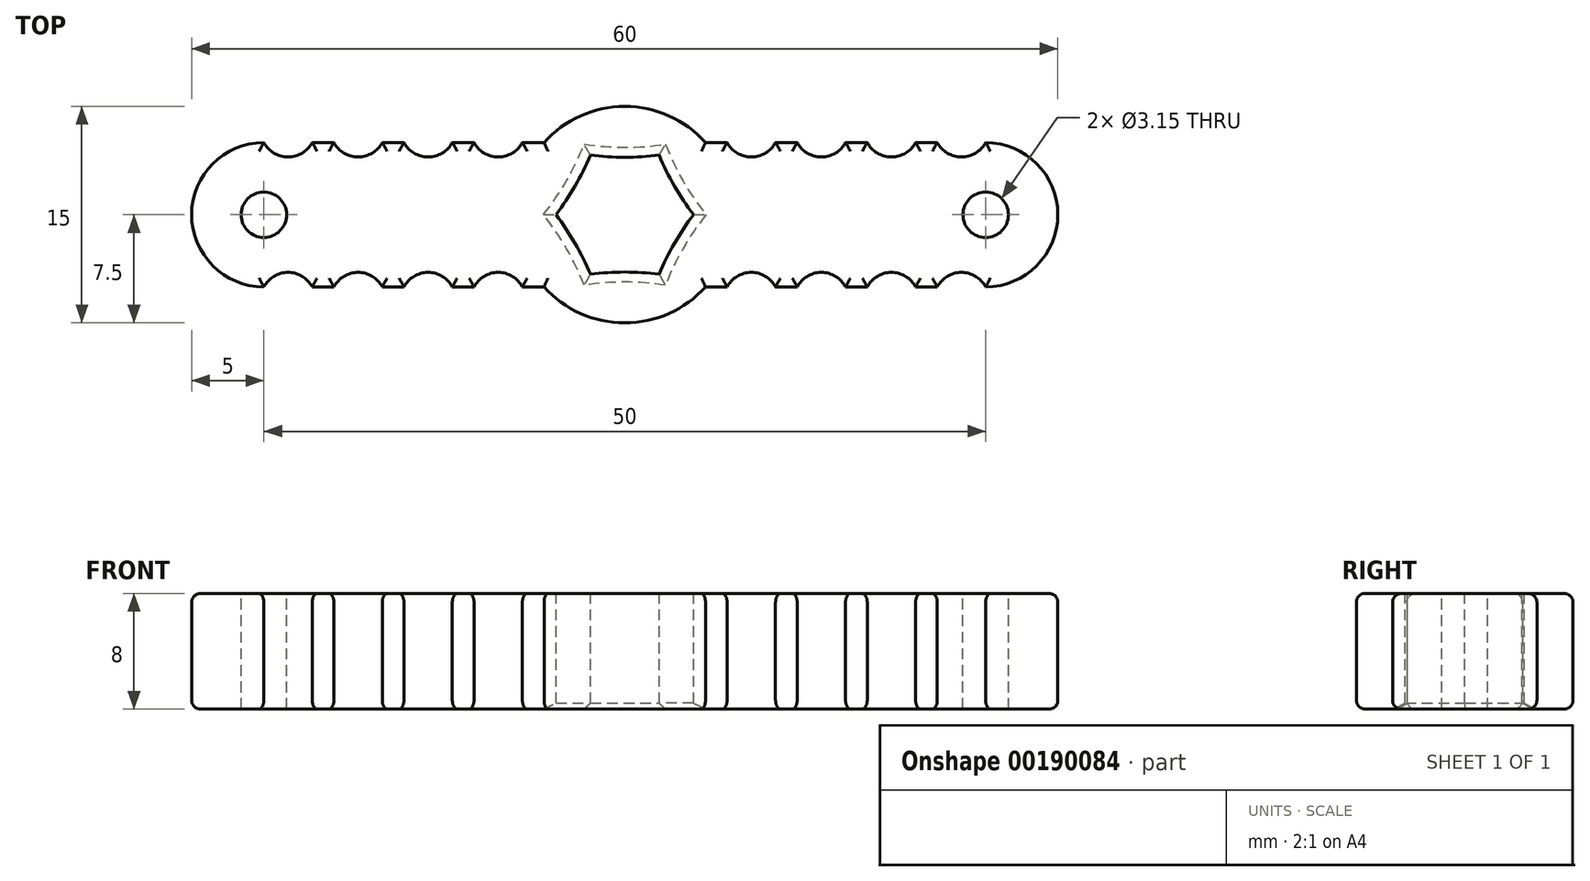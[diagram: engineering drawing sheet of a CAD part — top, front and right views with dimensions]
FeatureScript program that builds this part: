
annotation { "Feature Type Name" : "Feature", "Feature Type Description" : "" }
export const myFeature = defineFeature(function(context is Context, id is Id, definition is map)
    precondition{}
    {
        {
            var Q0;
            Q0=qCreatedBy(makeId("Top.planeOp"),FACE);
            var sketch = newSketch(context, id + "F0", { "sketchPlane" : qUnion([Q0])});
            skLineSegment(sketch, "E0", {"start": v(0, 7.5) * mm, "end": v(0, 0) * mm, "construction": true});
            skLineSegment(sketch, "E1", {"start": v(0, 0) * mm, "end": v(30, 0) * mm, "construction": true});
            skArc(sketch, "E2", {"start": v(30, 0) * mm, "mid": v(28.54, 3.54) * mm, "end": v(25, 5) * mm});
            skArc(sketch, "E3", {"start": v(5.6, 5) * mm, "mid": v(3.06, 6.85) * mm, "end": v(0, 7.5) * mm});
            skLineSegment(sketch, "E4", {"start": v(5.6, 5) * mm, "end": v(7.1, 5) * mm});
            skArc(sketch, "E5", {"start": v(7.1, 5) * mm, "mid": v(8.77, 4) * mm, "end": v(10.44, 5) * mm});
            skLineSegment(sketch, "E6.1.0.0", {"start": v(10.44, 5) * mm, "end": v(11.94, 5) * mm});
            skArc(sketch, "E6.1.0.1", {"start": v(11.94, 5) * mm, "mid": v(13.62, 4) * mm, "end": v(15.3, 5) * mm});
            skLineSegment(sketch, "E6.2.0.0", {"start": v(15.3, 5) * mm, "end": v(16.8, 5) * mm});
            skArc(sketch, "E6.2.0.1", {"start": v(16.8, 5) * mm, "mid": v(18.47, 4) * mm, "end": v(20.15, 5) * mm});
            skLineSegment(sketch, "E6.direction1", {"start": v(5.6, 5) * mm, "end": v(10.44, 5) * mm, "construction": true});
            skLineSegment(sketch, "E7.0.3.0", {"start": v(20.15, 5) * mm, "end": v(21.65, 5) * mm});
            skArc(sketch, "E7.3.3.0", {"start": v(21.65, 5) * mm, "mid": v(23.32, 4) * mm, "end": v(25, 5) * mm});
            skArc(sketch, "E8.MirrorCS", {"start": v(30, 0) * mm, "mid": v(28.54, -3.54) * mm, "end": v(25, -5) * mm});
            skArc(sketch, "E9.MirrorCS", {"start": v(21.65, -5) * mm, "mid": v(23.32, -4) * mm, "end": v(25, -5) * mm});
            skLineSegment(sketch, "E10.MirrorCS", {"start": v(20.15, -5) * mm, "end": v(21.65, -5) * mm});
            skArc(sketch, "E11.MirrorCS", {"start": v(16.8, -5) * mm, "mid": v(18.47, -4) * mm, "end": v(20.15, -5) * mm});
            skLineSegment(sketch, "E12.MirrorCS", {"start": v(15.3, -5) * mm, "end": v(16.8, -5) * mm});
            skArc(sketch, "E13.MirrorCS", {"start": v(11.94, -5) * mm, "mid": v(13.62, -4) * mm, "end": v(15.3, -5) * mm});
            skLineSegment(sketch, "E14.MirrorCS", {"start": v(10.44, -5) * mm, "end": v(11.94, -5) * mm});
            skLineSegment(sketch, "E15.MirrorCS", {"start": v(5.6, -5) * mm, "end": v(7.1, -5) * mm});
            skArc(sketch, "E16.MirrorCS", {"start": v(7.1, -5) * mm, "mid": v(8.77, -4) * mm, "end": v(10.44, -5) * mm});
            skArc(sketch, "E17.MirrorCS", {"start": v(5.6, -5) * mm, "mid": v(3.06, -6.85) * mm, "end": v(0, -7.5) * mm});
            skArc(sketch, "E18.MirrorCS", {"start": v(-5.6, 5) * mm, "mid": v(-3.06, 6.85) * mm, "end": v(0, 7.5) * mm});
            skLineSegment(sketch, "E19.MirrorCS", {"start": v(-5.6, 5) * mm, "end": v(-7.1, 5) * mm});
            skArc(sketch, "E20.MirrorCS", {"start": v(-7.1, 5) * mm, "mid": v(-8.77, 4) * mm, "end": v(-10.44, 5) * mm});
            skLineSegment(sketch, "E21.MirrorCS", {"start": v(-10.44, 5) * mm, "end": v(-11.94, 5) * mm});
            skArc(sketch, "E22.MirrorCS", {"start": v(-11.94, 5) * mm, "mid": v(-13.62, 4) * mm, "end": v(-15.3, 5) * mm});
            skLineSegment(sketch, "E23.MirrorCS", {"start": v(-15.3, 5) * mm, "end": v(-16.8, 5) * mm});
            skArc(sketch, "E24.MirrorCS", {"start": v(-16.8, 5) * mm, "mid": v(-18.47, 4) * mm, "end": v(-20.15, 5) * mm});
            skLineSegment(sketch, "E25.MirrorCS", {"start": v(-20.15, 5) * mm, "end": v(-21.65, 5) * mm});
            skArc(sketch, "E26.MirrorCS", {"start": v(-21.65, 5) * mm, "mid": v(-23.32, 4) * mm, "end": v(-25, 5) * mm});
            skArc(sketch, "E27.MirrorCS", {"start": v(-30, 0) * mm, "mid": v(-28.54, 3.54) * mm, "end": v(-25, 5) * mm});
            skArc(sketch, "E28.MirrorCS", {"start": v(-30, 0) * mm, "mid": v(-28.54, -3.54) * mm, "end": v(-25, -5) * mm});
            skArc(sketch, "E29.MirrorCS", {"start": v(-21.65, -5) * mm, "mid": v(-23.32, -4) * mm, "end": v(-25, -5) * mm});
            skLineSegment(sketch, "E30.MirrorCS", {"start": v(-20.15, -5) * mm, "end": v(-21.65, -5) * mm});
            skArc(sketch, "E31.MirrorCS", {"start": v(-16.8, -5) * mm, "mid": v(-18.47, -4) * mm, "end": v(-20.15, -5) * mm});
            skLineSegment(sketch, "E32.MirrorCS", {"start": v(-15.3, -5) * mm, "end": v(-16.8, -5) * mm});
            skArc(sketch, "E33.MirrorCS", {"start": v(-11.94, -5) * mm, "mid": v(-13.62, -4) * mm, "end": v(-15.3, -5) * mm});
            skLineSegment(sketch, "E34.MirrorCS", {"start": v(-10.44, -5) * mm, "end": v(-11.94, -5) * mm});
            skArc(sketch, "E35.MirrorCS", {"start": v(-7.1, -5) * mm, "mid": v(-8.77, -4) * mm, "end": v(-10.44, -5) * mm});
            skLineSegment(sketch, "E36.MirrorCS", {"start": v(-5.6, -5) * mm, "end": v(-7.1, -5) * mm});
            skArc(sketch, "E37.MirrorCS", {"start": v(-5.6, -5) * mm, "mid": v(-3.06, -6.85) * mm, "end": v(0, -7.5) * mm});
            skSolve(sketch);
        }
        {
            var Q0;
            Q0 = qSketchRegion(id + "F0", true);
            extrude(context, id + "F1", {"entities" : qUnion([Q0]), "depth" : 8 * mm});
        }
        {
            var Q0;
            Q0=makeQuery(id+"F1.opExtrude","CAP_FACE",FACE,{"disambiguationData":[OSD([sQuery(id+"F0.wireOp",EDGE,"E2"),sQuery(id+"F0.wireOp",EDGE,"E3"),sQuery(id+"F0.wireOp",EDGE,"E4"),sQuery(id+"F0.wireOp",EDGE,"E5"),sQuery(id+"F0.wireOp",EDGE,"E6.1.0.0"),sQuery(id+"F0.wireOp",EDGE,"E6.1.0.1"),sQuery(id+"F0.wireOp",EDGE,"E6.2.0.0"),sQuery(id+"F0.wireOp",EDGE,"E6.2.0.1"),sQuery(id+"F0.wireOp",EDGE,"E7.0.3.0"),sQuery(id+"F0.wireOp",EDGE,"E7.3.3.0"),sQuery(id+"F0.wireOp",EDGE,"E8.MirrorCS"),sQuery(id+"F0.wireOp",EDGE,"E9.MirrorCS"),sQuery(id+"F0.wireOp",EDGE,"E10.MirrorCS"),sQuery(id+"F0.wireOp",EDGE,"E11.MirrorCS"),sQuery(id+"F0.wireOp",EDGE,"E12.MirrorCS"),sQuery(id+"F0.wireOp",EDGE,"E13.MirrorCS"),sQuery(id+"F0.wireOp",EDGE,"E14.MirrorCS"),sQuery(id+"F0.wireOp",EDGE,"E15.MirrorCS"),sQuery(id+"F0.wireOp",EDGE,"E16.MirrorCS"),sQuery(id+"F0.wireOp",EDGE,"E17.MirrorCS"),sQuery(id+"F0.wireOp",EDGE,"E18.MirrorCS"),sQuery(id+"F0.wireOp",EDGE,"E19.MirrorCS"),sQuery(id+"F0.wireOp",EDGE,"E20.MirrorCS"),sQuery(id+"F0.wireOp",EDGE,"E21.MirrorCS"),sQuery(id+"F0.wireOp",EDGE,"E22.MirrorCS"),sQuery(id+"F0.wireOp",EDGE,"E23.MirrorCS"),sQuery(id+"F0.wireOp",EDGE,"E24.MirrorCS"),sQuery(id+"F0.wireOp",EDGE,"E25.MirrorCS"),sQuery(id+"F0.wireOp",EDGE,"E26.MirrorCS"),sQuery(id+"F0.wireOp",EDGE,"E27.MirrorCS"),sQuery(id+"F0.wireOp",EDGE,"E28.MirrorCS"),sQuery(id+"F0.wireOp",EDGE,"E29.MirrorCS"),sQuery(id+"F0.wireOp",EDGE,"E30.MirrorCS"),sQuery(id+"F0.wireOp",EDGE,"E31.MirrorCS"),sQuery(id+"F0.wireOp",EDGE,"E32.MirrorCS"),sQuery(id+"F0.wireOp",EDGE,"E33.MirrorCS"),sQuery(id+"F0.wireOp",EDGE,"E34.MirrorCS"),sQuery(id+"F0.wireOp",EDGE,"E35.MirrorCS"),sQuery(id+"F0.wireOp",EDGE,"E36.MirrorCS"),sQuery(id+"F0.wireOp",EDGE,"E37.MirrorCS")])],"isStart":false});
            var Q1;
            Q1=makeQuery(id+"F1.opExtrude","CAP_FACE",FACE,{"disambiguationData":[OSD([sQuery(id+"F0.wireOp",EDGE,"E2"),sQuery(id+"F0.wireOp",EDGE,"E3"),sQuery(id+"F0.wireOp",EDGE,"E4"),sQuery(id+"F0.wireOp",EDGE,"E5"),sQuery(id+"F0.wireOp",EDGE,"E6.1.0.0"),sQuery(id+"F0.wireOp",EDGE,"E6.1.0.1"),sQuery(id+"F0.wireOp",EDGE,"E6.2.0.0"),sQuery(id+"F0.wireOp",EDGE,"E6.2.0.1"),sQuery(id+"F0.wireOp",EDGE,"E7.0.3.0"),sQuery(id+"F0.wireOp",EDGE,"E7.3.3.0"),sQuery(id+"F0.wireOp",EDGE,"E8.MirrorCS"),sQuery(id+"F0.wireOp",EDGE,"E9.MirrorCS"),sQuery(id+"F0.wireOp",EDGE,"E10.MirrorCS"),sQuery(id+"F0.wireOp",EDGE,"E11.MirrorCS"),sQuery(id+"F0.wireOp",EDGE,"E12.MirrorCS"),sQuery(id+"F0.wireOp",EDGE,"E13.MirrorCS"),sQuery(id+"F0.wireOp",EDGE,"E14.MirrorCS"),sQuery(id+"F0.wireOp",EDGE,"E15.MirrorCS"),sQuery(id+"F0.wireOp",EDGE,"E16.MirrorCS"),sQuery(id+"F0.wireOp",EDGE,"E17.MirrorCS"),sQuery(id+"F0.wireOp",EDGE,"E18.MirrorCS"),sQuery(id+"F0.wireOp",EDGE,"E19.MirrorCS"),sQuery(id+"F0.wireOp",EDGE,"E20.MirrorCS"),sQuery(id+"F0.wireOp",EDGE,"E21.MirrorCS"),sQuery(id+"F0.wireOp",EDGE,"E22.MirrorCS"),sQuery(id+"F0.wireOp",EDGE,"E23.MirrorCS"),sQuery(id+"F0.wireOp",EDGE,"E24.MirrorCS"),sQuery(id+"F0.wireOp",EDGE,"E25.MirrorCS"),sQuery(id+"F0.wireOp",EDGE,"E26.MirrorCS"),sQuery(id+"F0.wireOp",EDGE,"E27.MirrorCS"),sQuery(id+"F0.wireOp",EDGE,"E28.MirrorCS"),sQuery(id+"F0.wireOp",EDGE,"E29.MirrorCS"),sQuery(id+"F0.wireOp",EDGE,"E30.MirrorCS"),sQuery(id+"F0.wireOp",EDGE,"E31.MirrorCS"),sQuery(id+"F0.wireOp",EDGE,"E32.MirrorCS"),sQuery(id+"F0.wireOp",EDGE,"E33.MirrorCS"),sQuery(id+"F0.wireOp",EDGE,"E34.MirrorCS"),sQuery(id+"F0.wireOp",EDGE,"E35.MirrorCS"),sQuery(id+"F0.wireOp",EDGE,"E36.MirrorCS"),sQuery(id+"F0.wireOp",EDGE,"E37.MirrorCS")])],"isStart":true});
            fillet(context, id + "F2", {"entities" : qUnion([Q0, Q1]), "radius" : 0.6 * mm, "tangentPropagation" : true, "allowEdgeOverflow" : false});
        }
        {
            var Q0;
            Q0=makeQuery(id+"F1.opExtrude","CAP_FACE",FACE,{"disambiguationData":[OSD([sQuery(id+"F0.wireOp",EDGE,"E2"),sQuery(id+"F0.wireOp",EDGE,"E3"),sQuery(id+"F0.wireOp",EDGE,"E4"),sQuery(id+"F0.wireOp",EDGE,"E5"),sQuery(id+"F0.wireOp",EDGE,"E6.1.0.0"),sQuery(id+"F0.wireOp",EDGE,"E6.1.0.1"),sQuery(id+"F0.wireOp",EDGE,"E6.2.0.0"),sQuery(id+"F0.wireOp",EDGE,"E6.2.0.1"),sQuery(id+"F0.wireOp",EDGE,"E7.0.3.0"),sQuery(id+"F0.wireOp",EDGE,"E7.3.3.0"),sQuery(id+"F0.wireOp",EDGE,"E8.MirrorCS"),sQuery(id+"F0.wireOp",EDGE,"E9.MirrorCS"),sQuery(id+"F0.wireOp",EDGE,"E10.MirrorCS"),sQuery(id+"F0.wireOp",EDGE,"E11.MirrorCS"),sQuery(id+"F0.wireOp",EDGE,"E12.MirrorCS"),sQuery(id+"F0.wireOp",EDGE,"E13.MirrorCS"),sQuery(id+"F0.wireOp",EDGE,"E14.MirrorCS"),sQuery(id+"F0.wireOp",EDGE,"E15.MirrorCS"),sQuery(id+"F0.wireOp",EDGE,"E16.MirrorCS"),sQuery(id+"F0.wireOp",EDGE,"E17.MirrorCS"),sQuery(id+"F0.wireOp",EDGE,"E18.MirrorCS"),sQuery(id+"F0.wireOp",EDGE,"E19.MirrorCS"),sQuery(id+"F0.wireOp",EDGE,"E20.MirrorCS"),sQuery(id+"F0.wireOp",EDGE,"E21.MirrorCS"),sQuery(id+"F0.wireOp",EDGE,"E22.MirrorCS"),sQuery(id+"F0.wireOp",EDGE,"E23.MirrorCS"),sQuery(id+"F0.wireOp",EDGE,"E24.MirrorCS"),sQuery(id+"F0.wireOp",EDGE,"E25.MirrorCS"),sQuery(id+"F0.wireOp",EDGE,"E26.MirrorCS"),sQuery(id+"F0.wireOp",EDGE,"E27.MirrorCS"),sQuery(id+"F0.wireOp",EDGE,"E28.MirrorCS"),sQuery(id+"F0.wireOp",EDGE,"E29.MirrorCS"),sQuery(id+"F0.wireOp",EDGE,"E30.MirrorCS"),sQuery(id+"F0.wireOp",EDGE,"E31.MirrorCS"),sQuery(id+"F0.wireOp",EDGE,"E32.MirrorCS"),sQuery(id+"F0.wireOp",EDGE,"E33.MirrorCS"),sQuery(id+"F0.wireOp",EDGE,"E34.MirrorCS"),sQuery(id+"F0.wireOp",EDGE,"E35.MirrorCS"),sQuery(id+"F0.wireOp",EDGE,"E36.MirrorCS"),sQuery(id+"F0.wireOp",EDGE,"E37.MirrorCS")])],"isStart":false});
            var sketch = newSketch(context, id + "F3", { "sketchPlane" : qUnion([Q0])});
            skCircle(sketch, "E38", {"center": v(0, 0) * mm, "radius": 3.98 * mm, "construction": true});
            skLineSegment(sketch, "E39", {"start": v(0, 0) * mm, "end": v(0, 3.98) * mm, "construction": true});
            skArc(sketch, "E40", {"start": v(-2.38, 4.12) * mm, "mid": v(0, 3.97) * mm, "end": v(2.38, 4.13) * mm});
            skArc(sketch, "E41.1.0", {"start": v(-4.76, 0) * mm, "mid": v(-3.44, 1.99) * mm, "end": v(-2.38, 4.12) * mm});
            skArc(sketch, "E41.2.0", {"start": v(-2.38, -4.12) * mm, "mid": v(-3.44, -1.99) * mm, "end": v(-4.76, 0) * mm});
            skArc(sketch, "E41.3.0", {"start": v(2.38, -4.13) * mm, "mid": v(0, -3.97) * mm, "end": v(-2.38, -4.12) * mm});
            skArc(sketch, "E41.4.0", {"start": v(4.76, 0) * mm, "mid": v(3.44, -1.99) * mm, "end": v(2.38, -4.12) * mm});
            skArc(sketch, "E41.5.0", {"start": v(2.38, 4.13) * mm, "mid": v(3.44, 1.99) * mm, "end": v(4.76, 0) * mm});
            skSolve(sketch);
        }
        {
            var Q0;
            Q0 = qSketchRegion(id + "F3", true);
            extrude(context, id + "F4", {"entities" : qUnion([Q0]), "operationType" : NewBodyOperationType.REMOVE, "endBound" : BoundingType.THROUGH_ALL, "oppositeDirection" : true, "depth" : 25 * mm});
        }
        {
            var Q0;
            Q0=makeQuery(id+"F4.boolean.opBoolean","INTERSECT",EDGE,{"derivedFrom":[makeQuery(id+"F1.opExtrude","CAP_FACE",FACE,{"disambiguationData":[OSD([sQuery(id+"F0.wireOp",EDGE,"E2"),sQuery(id+"F0.wireOp",EDGE,"E3"),sQuery(id+"F0.wireOp",EDGE,"E4"),sQuery(id+"F0.wireOp",EDGE,"E5"),sQuery(id+"F0.wireOp",EDGE,"E6.1.0.0"),sQuery(id+"F0.wireOp",EDGE,"E6.1.0.1"),sQuery(id+"F0.wireOp",EDGE,"E6.2.0.0"),sQuery(id+"F0.wireOp",EDGE,"E6.2.0.1"),sQuery(id+"F0.wireOp",EDGE,"E7.0.3.0"),sQuery(id+"F0.wireOp",EDGE,"E7.3.3.0"),sQuery(id+"F0.wireOp",EDGE,"E8.MirrorCS"),sQuery(id+"F0.wireOp",EDGE,"E9.MirrorCS"),sQuery(id+"F0.wireOp",EDGE,"E10.MirrorCS"),sQuery(id+"F0.wireOp",EDGE,"E11.MirrorCS"),sQuery(id+"F0.wireOp",EDGE,"E12.MirrorCS"),sQuery(id+"F0.wireOp",EDGE,"E13.MirrorCS"),sQuery(id+"F0.wireOp",EDGE,"E14.MirrorCS"),sQuery(id+"F0.wireOp",EDGE,"E15.MirrorCS"),sQuery(id+"F0.wireOp",EDGE,"E16.MirrorCS"),sQuery(id+"F0.wireOp",EDGE,"E17.MirrorCS"),sQuery(id+"F0.wireOp",EDGE,"E18.MirrorCS"),sQuery(id+"F0.wireOp",EDGE,"E19.MirrorCS"),sQuery(id+"F0.wireOp",EDGE,"E20.MirrorCS"),sQuery(id+"F0.wireOp",EDGE,"E21.MirrorCS"),sQuery(id+"F0.wireOp",EDGE,"E22.MirrorCS"),sQuery(id+"F0.wireOp",EDGE,"E23.MirrorCS"),sQuery(id+"F0.wireOp",EDGE,"E24.MirrorCS"),sQuery(id+"F0.wireOp",EDGE,"E25.MirrorCS"),sQuery(id+"F0.wireOp",EDGE,"E26.MirrorCS"),sQuery(id+"F0.wireOp",EDGE,"E27.MirrorCS"),sQuery(id+"F0.wireOp",EDGE,"E28.MirrorCS"),sQuery(id+"F0.wireOp",EDGE,"E29.MirrorCS"),sQuery(id+"F0.wireOp",EDGE,"E30.MirrorCS"),sQuery(id+"F0.wireOp",EDGE,"E31.MirrorCS"),sQuery(id+"F0.wireOp",EDGE,"E32.MirrorCS"),sQuery(id+"F0.wireOp",EDGE,"E33.MirrorCS"),sQuery(id+"F0.wireOp",EDGE,"E34.MirrorCS"),sQuery(id+"F0.wireOp",EDGE,"E35.MirrorCS"),sQuery(id+"F0.wireOp",EDGE,"E36.MirrorCS"),sQuery(id+"F0.wireOp",EDGE,"E37.MirrorCS")])],"isStart":true}),makeQuery(id+"F4.opExtrude","SWEPT_FACE",FACE,{"disambiguationData":[OSD([sQuery(id+"F3.wireOp",EDGE,"E41.2.0")])]})]});
            var Q1;
            Q1=makeQuery(id+"F4.boolean.opBoolean","INTERSECT",EDGE,{"derivedFrom":[makeQuery(id+"F1.opExtrude","CAP_FACE",FACE,{"disambiguationData":[OSD([sQuery(id+"F0.wireOp",EDGE,"E2"),sQuery(id+"F0.wireOp",EDGE,"E3"),sQuery(id+"F0.wireOp",EDGE,"E4"),sQuery(id+"F0.wireOp",EDGE,"E5"),sQuery(id+"F0.wireOp",EDGE,"E6.1.0.0"),sQuery(id+"F0.wireOp",EDGE,"E6.1.0.1"),sQuery(id+"F0.wireOp",EDGE,"E6.2.0.0"),sQuery(id+"F0.wireOp",EDGE,"E6.2.0.1"),sQuery(id+"F0.wireOp",EDGE,"E7.0.3.0"),sQuery(id+"F0.wireOp",EDGE,"E7.3.3.0"),sQuery(id+"F0.wireOp",EDGE,"E8.MirrorCS"),sQuery(id+"F0.wireOp",EDGE,"E9.MirrorCS"),sQuery(id+"F0.wireOp",EDGE,"E10.MirrorCS"),sQuery(id+"F0.wireOp",EDGE,"E11.MirrorCS"),sQuery(id+"F0.wireOp",EDGE,"E12.MirrorCS"),sQuery(id+"F0.wireOp",EDGE,"E13.MirrorCS"),sQuery(id+"F0.wireOp",EDGE,"E14.MirrorCS"),sQuery(id+"F0.wireOp",EDGE,"E15.MirrorCS"),sQuery(id+"F0.wireOp",EDGE,"E16.MirrorCS"),sQuery(id+"F0.wireOp",EDGE,"E17.MirrorCS"),sQuery(id+"F0.wireOp",EDGE,"E18.MirrorCS"),sQuery(id+"F0.wireOp",EDGE,"E19.MirrorCS"),sQuery(id+"F0.wireOp",EDGE,"E20.MirrorCS"),sQuery(id+"F0.wireOp",EDGE,"E21.MirrorCS"),sQuery(id+"F0.wireOp",EDGE,"E22.MirrorCS"),sQuery(id+"F0.wireOp",EDGE,"E23.MirrorCS"),sQuery(id+"F0.wireOp",EDGE,"E24.MirrorCS"),sQuery(id+"F0.wireOp",EDGE,"E25.MirrorCS"),sQuery(id+"F0.wireOp",EDGE,"E26.MirrorCS"),sQuery(id+"F0.wireOp",EDGE,"E27.MirrorCS"),sQuery(id+"F0.wireOp",EDGE,"E28.MirrorCS"),sQuery(id+"F0.wireOp",EDGE,"E29.MirrorCS"),sQuery(id+"F0.wireOp",EDGE,"E30.MirrorCS"),sQuery(id+"F0.wireOp",EDGE,"E31.MirrorCS"),sQuery(id+"F0.wireOp",EDGE,"E32.MirrorCS"),sQuery(id+"F0.wireOp",EDGE,"E33.MirrorCS"),sQuery(id+"F0.wireOp",EDGE,"E34.MirrorCS"),sQuery(id+"F0.wireOp",EDGE,"E35.MirrorCS"),sQuery(id+"F0.wireOp",EDGE,"E36.MirrorCS"),sQuery(id+"F0.wireOp",EDGE,"E37.MirrorCS")])],"isStart":true}),makeQuery(id+"F4.opExtrude","SWEPT_FACE",FACE,{"disambiguationData":[OSD([sQuery(id+"F3.wireOp",EDGE,"E41.3.0")])]})]});
            var Q2;
            Q2=makeQuery(id+"F4.boolean.opBoolean","INTERSECT",EDGE,{"derivedFrom":[makeQuery(id+"F1.opExtrude","CAP_FACE",FACE,{"disambiguationData":[OSD([sQuery(id+"F0.wireOp",EDGE,"E2"),sQuery(id+"F0.wireOp",EDGE,"E3"),sQuery(id+"F0.wireOp",EDGE,"E4"),sQuery(id+"F0.wireOp",EDGE,"E5"),sQuery(id+"F0.wireOp",EDGE,"E6.1.0.0"),sQuery(id+"F0.wireOp",EDGE,"E6.1.0.1"),sQuery(id+"F0.wireOp",EDGE,"E6.2.0.0"),sQuery(id+"F0.wireOp",EDGE,"E6.2.0.1"),sQuery(id+"F0.wireOp",EDGE,"E7.0.3.0"),sQuery(id+"F0.wireOp",EDGE,"E7.3.3.0"),sQuery(id+"F0.wireOp",EDGE,"E8.MirrorCS"),sQuery(id+"F0.wireOp",EDGE,"E9.MirrorCS"),sQuery(id+"F0.wireOp",EDGE,"E10.MirrorCS"),sQuery(id+"F0.wireOp",EDGE,"E11.MirrorCS"),sQuery(id+"F0.wireOp",EDGE,"E12.MirrorCS"),sQuery(id+"F0.wireOp",EDGE,"E13.MirrorCS"),sQuery(id+"F0.wireOp",EDGE,"E14.MirrorCS"),sQuery(id+"F0.wireOp",EDGE,"E15.MirrorCS"),sQuery(id+"F0.wireOp",EDGE,"E16.MirrorCS"),sQuery(id+"F0.wireOp",EDGE,"E17.MirrorCS"),sQuery(id+"F0.wireOp",EDGE,"E18.MirrorCS"),sQuery(id+"F0.wireOp",EDGE,"E19.MirrorCS"),sQuery(id+"F0.wireOp",EDGE,"E20.MirrorCS"),sQuery(id+"F0.wireOp",EDGE,"E21.MirrorCS"),sQuery(id+"F0.wireOp",EDGE,"E22.MirrorCS"),sQuery(id+"F0.wireOp",EDGE,"E23.MirrorCS"),sQuery(id+"F0.wireOp",EDGE,"E24.MirrorCS"),sQuery(id+"F0.wireOp",EDGE,"E25.MirrorCS"),sQuery(id+"F0.wireOp",EDGE,"E26.MirrorCS"),sQuery(id+"F0.wireOp",EDGE,"E27.MirrorCS"),sQuery(id+"F0.wireOp",EDGE,"E28.MirrorCS"),sQuery(id+"F0.wireOp",EDGE,"E29.MirrorCS"),sQuery(id+"F0.wireOp",EDGE,"E30.MirrorCS"),sQuery(id+"F0.wireOp",EDGE,"E31.MirrorCS"),sQuery(id+"F0.wireOp",EDGE,"E32.MirrorCS"),sQuery(id+"F0.wireOp",EDGE,"E33.MirrorCS"),sQuery(id+"F0.wireOp",EDGE,"E34.MirrorCS"),sQuery(id+"F0.wireOp",EDGE,"E35.MirrorCS"),sQuery(id+"F0.wireOp",EDGE,"E36.MirrorCS"),sQuery(id+"F0.wireOp",EDGE,"E37.MirrorCS")])],"isStart":true}),makeQuery(id+"F4.opExtrude","SWEPT_FACE",FACE,{"disambiguationData":[OSD([sQuery(id+"F3.wireOp",EDGE,"E41.4.0")])]})]});
            var Q3;
            Q3=makeQuery(id+"F4.boolean.opBoolean","INTERSECT",EDGE,{"derivedFrom":[makeQuery(id+"F1.opExtrude","CAP_FACE",FACE,{"disambiguationData":[OSD([sQuery(id+"F0.wireOp",EDGE,"E2"),sQuery(id+"F0.wireOp",EDGE,"E3"),sQuery(id+"F0.wireOp",EDGE,"E4"),sQuery(id+"F0.wireOp",EDGE,"E5"),sQuery(id+"F0.wireOp",EDGE,"E6.1.0.0"),sQuery(id+"F0.wireOp",EDGE,"E6.1.0.1"),sQuery(id+"F0.wireOp",EDGE,"E6.2.0.0"),sQuery(id+"F0.wireOp",EDGE,"E6.2.0.1"),sQuery(id+"F0.wireOp",EDGE,"E7.0.3.0"),sQuery(id+"F0.wireOp",EDGE,"E7.3.3.0"),sQuery(id+"F0.wireOp",EDGE,"E8.MirrorCS"),sQuery(id+"F0.wireOp",EDGE,"E9.MirrorCS"),sQuery(id+"F0.wireOp",EDGE,"E10.MirrorCS"),sQuery(id+"F0.wireOp",EDGE,"E11.MirrorCS"),sQuery(id+"F0.wireOp",EDGE,"E12.MirrorCS"),sQuery(id+"F0.wireOp",EDGE,"E13.MirrorCS"),sQuery(id+"F0.wireOp",EDGE,"E14.MirrorCS"),sQuery(id+"F0.wireOp",EDGE,"E15.MirrorCS"),sQuery(id+"F0.wireOp",EDGE,"E16.MirrorCS"),sQuery(id+"F0.wireOp",EDGE,"E17.MirrorCS"),sQuery(id+"F0.wireOp",EDGE,"E18.MirrorCS"),sQuery(id+"F0.wireOp",EDGE,"E19.MirrorCS"),sQuery(id+"F0.wireOp",EDGE,"E20.MirrorCS"),sQuery(id+"F0.wireOp",EDGE,"E21.MirrorCS"),sQuery(id+"F0.wireOp",EDGE,"E22.MirrorCS"),sQuery(id+"F0.wireOp",EDGE,"E23.MirrorCS"),sQuery(id+"F0.wireOp",EDGE,"E24.MirrorCS"),sQuery(id+"F0.wireOp",EDGE,"E25.MirrorCS"),sQuery(id+"F0.wireOp",EDGE,"E26.MirrorCS"),sQuery(id+"F0.wireOp",EDGE,"E27.MirrorCS"),sQuery(id+"F0.wireOp",EDGE,"E28.MirrorCS"),sQuery(id+"F0.wireOp",EDGE,"E29.MirrorCS"),sQuery(id+"F0.wireOp",EDGE,"E30.MirrorCS"),sQuery(id+"F0.wireOp",EDGE,"E31.MirrorCS"),sQuery(id+"F0.wireOp",EDGE,"E32.MirrorCS"),sQuery(id+"F0.wireOp",EDGE,"E33.MirrorCS"),sQuery(id+"F0.wireOp",EDGE,"E34.MirrorCS"),sQuery(id+"F0.wireOp",EDGE,"E35.MirrorCS"),sQuery(id+"F0.wireOp",EDGE,"E36.MirrorCS"),sQuery(id+"F0.wireOp",EDGE,"E37.MirrorCS")])],"isStart":true}),makeQuery(id+"F4.opExtrude","SWEPT_FACE",FACE,{"disambiguationData":[OSD([sQuery(id+"F3.wireOp",EDGE,"E41.5.0")])]})]});
            var Q4;
            Q4=makeQuery(id+"F4.boolean.opBoolean","INTERSECT",EDGE,{"derivedFrom":[makeQuery(id+"F1.opExtrude","CAP_FACE",FACE,{"disambiguationData":[OSD([sQuery(id+"F0.wireOp",EDGE,"E2"),sQuery(id+"F0.wireOp",EDGE,"E3"),sQuery(id+"F0.wireOp",EDGE,"E4"),sQuery(id+"F0.wireOp",EDGE,"E5"),sQuery(id+"F0.wireOp",EDGE,"E6.1.0.0"),sQuery(id+"F0.wireOp",EDGE,"E6.1.0.1"),sQuery(id+"F0.wireOp",EDGE,"E6.2.0.0"),sQuery(id+"F0.wireOp",EDGE,"E6.2.0.1"),sQuery(id+"F0.wireOp",EDGE,"E7.0.3.0"),sQuery(id+"F0.wireOp",EDGE,"E7.3.3.0"),sQuery(id+"F0.wireOp",EDGE,"E8.MirrorCS"),sQuery(id+"F0.wireOp",EDGE,"E9.MirrorCS"),sQuery(id+"F0.wireOp",EDGE,"E10.MirrorCS"),sQuery(id+"F0.wireOp",EDGE,"E11.MirrorCS"),sQuery(id+"F0.wireOp",EDGE,"E12.MirrorCS"),sQuery(id+"F0.wireOp",EDGE,"E13.MirrorCS"),sQuery(id+"F0.wireOp",EDGE,"E14.MirrorCS"),sQuery(id+"F0.wireOp",EDGE,"E15.MirrorCS"),sQuery(id+"F0.wireOp",EDGE,"E16.MirrorCS"),sQuery(id+"F0.wireOp",EDGE,"E17.MirrorCS"),sQuery(id+"F0.wireOp",EDGE,"E18.MirrorCS"),sQuery(id+"F0.wireOp",EDGE,"E19.MirrorCS"),sQuery(id+"F0.wireOp",EDGE,"E20.MirrorCS"),sQuery(id+"F0.wireOp",EDGE,"E21.MirrorCS"),sQuery(id+"F0.wireOp",EDGE,"E22.MirrorCS"),sQuery(id+"F0.wireOp",EDGE,"E23.MirrorCS"),sQuery(id+"F0.wireOp",EDGE,"E24.MirrorCS"),sQuery(id+"F0.wireOp",EDGE,"E25.MirrorCS"),sQuery(id+"F0.wireOp",EDGE,"E26.MirrorCS"),sQuery(id+"F0.wireOp",EDGE,"E27.MirrorCS"),sQuery(id+"F0.wireOp",EDGE,"E28.MirrorCS"),sQuery(id+"F0.wireOp",EDGE,"E29.MirrorCS"),sQuery(id+"F0.wireOp",EDGE,"E30.MirrorCS"),sQuery(id+"F0.wireOp",EDGE,"E31.MirrorCS"),sQuery(id+"F0.wireOp",EDGE,"E32.MirrorCS"),sQuery(id+"F0.wireOp",EDGE,"E33.MirrorCS"),sQuery(id+"F0.wireOp",EDGE,"E34.MirrorCS"),sQuery(id+"F0.wireOp",EDGE,"E35.MirrorCS"),sQuery(id+"F0.wireOp",EDGE,"E36.MirrorCS"),sQuery(id+"F0.wireOp",EDGE,"E37.MirrorCS")])],"isStart":true}),makeQuery(id+"F4.opExtrude","SWEPT_FACE",FACE,{"disambiguationData":[OSD([sQuery(id+"F3.wireOp",EDGE,"E40")])]})]});
            var Q5;
            Q5=makeQuery(id+"F4.boolean.opBoolean","INTERSECT",EDGE,{"derivedFrom":[makeQuery(id+"F1.opExtrude","CAP_FACE",FACE,{"disambiguationData":[OSD([sQuery(id+"F0.wireOp",EDGE,"E2"),sQuery(id+"F0.wireOp",EDGE,"E3"),sQuery(id+"F0.wireOp",EDGE,"E4"),sQuery(id+"F0.wireOp",EDGE,"E5"),sQuery(id+"F0.wireOp",EDGE,"E6.1.0.0"),sQuery(id+"F0.wireOp",EDGE,"E6.1.0.1"),sQuery(id+"F0.wireOp",EDGE,"E6.2.0.0"),sQuery(id+"F0.wireOp",EDGE,"E6.2.0.1"),sQuery(id+"F0.wireOp",EDGE,"E7.0.3.0"),sQuery(id+"F0.wireOp",EDGE,"E7.3.3.0"),sQuery(id+"F0.wireOp",EDGE,"E8.MirrorCS"),sQuery(id+"F0.wireOp",EDGE,"E9.MirrorCS"),sQuery(id+"F0.wireOp",EDGE,"E10.MirrorCS"),sQuery(id+"F0.wireOp",EDGE,"E11.MirrorCS"),sQuery(id+"F0.wireOp",EDGE,"E12.MirrorCS"),sQuery(id+"F0.wireOp",EDGE,"E13.MirrorCS"),sQuery(id+"F0.wireOp",EDGE,"E14.MirrorCS"),sQuery(id+"F0.wireOp",EDGE,"E15.MirrorCS"),sQuery(id+"F0.wireOp",EDGE,"E16.MirrorCS"),sQuery(id+"F0.wireOp",EDGE,"E17.MirrorCS"),sQuery(id+"F0.wireOp",EDGE,"E18.MirrorCS"),sQuery(id+"F0.wireOp",EDGE,"E19.MirrorCS"),sQuery(id+"F0.wireOp",EDGE,"E20.MirrorCS"),sQuery(id+"F0.wireOp",EDGE,"E21.MirrorCS"),sQuery(id+"F0.wireOp",EDGE,"E22.MirrorCS"),sQuery(id+"F0.wireOp",EDGE,"E23.MirrorCS"),sQuery(id+"F0.wireOp",EDGE,"E24.MirrorCS"),sQuery(id+"F0.wireOp",EDGE,"E25.MirrorCS"),sQuery(id+"F0.wireOp",EDGE,"E26.MirrorCS"),sQuery(id+"F0.wireOp",EDGE,"E27.MirrorCS"),sQuery(id+"F0.wireOp",EDGE,"E28.MirrorCS"),sQuery(id+"F0.wireOp",EDGE,"E29.MirrorCS"),sQuery(id+"F0.wireOp",EDGE,"E30.MirrorCS"),sQuery(id+"F0.wireOp",EDGE,"E31.MirrorCS"),sQuery(id+"F0.wireOp",EDGE,"E32.MirrorCS"),sQuery(id+"F0.wireOp",EDGE,"E33.MirrorCS"),sQuery(id+"F0.wireOp",EDGE,"E34.MirrorCS"),sQuery(id+"F0.wireOp",EDGE,"E35.MirrorCS"),sQuery(id+"F0.wireOp",EDGE,"E36.MirrorCS"),sQuery(id+"F0.wireOp",EDGE,"E37.MirrorCS")])],"isStart":true}),makeQuery(id+"F4.opExtrude","SWEPT_FACE",FACE,{"disambiguationData":[OSD([sQuery(id+"F3.wireOp",EDGE,"E41.1.0")])]})]});
            chamfer(context, id + "F5", {"entities" : qUnion([Q0, Q1, Q2, Q3, Q4, Q5]), "chamferType" : ChamferType.OFFSET_ANGLE, "width" : 0.4 * mm, "oppositeDirection" : false, "angle" : 60 * degree, "tangentPropagation" : true});
        }
        {
            var Q0;
            Q0=makeQuery(id+"F1.opExtrude","CAP_FACE",FACE,{"disambiguationData":[OSD([sQuery(id+"F0.wireOp",EDGE,"E2"),sQuery(id+"F0.wireOp",EDGE,"E3"),sQuery(id+"F0.wireOp",EDGE,"E4"),sQuery(id+"F0.wireOp",EDGE,"E5"),sQuery(id+"F0.wireOp",EDGE,"E6.1.0.0"),sQuery(id+"F0.wireOp",EDGE,"E6.1.0.1"),sQuery(id+"F0.wireOp",EDGE,"E6.2.0.0"),sQuery(id+"F0.wireOp",EDGE,"E6.2.0.1"),sQuery(id+"F0.wireOp",EDGE,"E7.0.3.0"),sQuery(id+"F0.wireOp",EDGE,"E7.3.3.0"),sQuery(id+"F0.wireOp",EDGE,"E8.MirrorCS"),sQuery(id+"F0.wireOp",EDGE,"E9.MirrorCS"),sQuery(id+"F0.wireOp",EDGE,"E10.MirrorCS"),sQuery(id+"F0.wireOp",EDGE,"E11.MirrorCS"),sQuery(id+"F0.wireOp",EDGE,"E12.MirrorCS"),sQuery(id+"F0.wireOp",EDGE,"E13.MirrorCS"),sQuery(id+"F0.wireOp",EDGE,"E14.MirrorCS"),sQuery(id+"F0.wireOp",EDGE,"E15.MirrorCS"),sQuery(id+"F0.wireOp",EDGE,"E16.MirrorCS"),sQuery(id+"F0.wireOp",EDGE,"E17.MirrorCS"),sQuery(id+"F0.wireOp",EDGE,"E18.MirrorCS"),sQuery(id+"F0.wireOp",EDGE,"E19.MirrorCS"),sQuery(id+"F0.wireOp",EDGE,"E20.MirrorCS"),sQuery(id+"F0.wireOp",EDGE,"E21.MirrorCS"),sQuery(id+"F0.wireOp",EDGE,"E22.MirrorCS"),sQuery(id+"F0.wireOp",EDGE,"E23.MirrorCS"),sQuery(id+"F0.wireOp",EDGE,"E24.MirrorCS"),sQuery(id+"F0.wireOp",EDGE,"E25.MirrorCS"),sQuery(id+"F0.wireOp",EDGE,"E26.MirrorCS"),sQuery(id+"F0.wireOp",EDGE,"E27.MirrorCS"),sQuery(id+"F0.wireOp",EDGE,"E28.MirrorCS"),sQuery(id+"F0.wireOp",EDGE,"E29.MirrorCS"),sQuery(id+"F0.wireOp",EDGE,"E30.MirrorCS"),sQuery(id+"F0.wireOp",EDGE,"E31.MirrorCS"),sQuery(id+"F0.wireOp",EDGE,"E32.MirrorCS"),sQuery(id+"F0.wireOp",EDGE,"E33.MirrorCS"),sQuery(id+"F0.wireOp",EDGE,"E34.MirrorCS"),sQuery(id+"F0.wireOp",EDGE,"E35.MirrorCS"),sQuery(id+"F0.wireOp",EDGE,"E36.MirrorCS"),sQuery(id+"F0.wireOp",EDGE,"E37.MirrorCS")])],"isStart":false});
            var sketch = newSketch(context, id + "F6", { "sketchPlane" : qUnion([Q0])});
            skPoint(sketch, "E42", {"position": v(-25, 0) * mm});
            skPoint(sketch, "E43", {"position": v(25, 0) * mm});
            skSolve(sketch);
        }
        {
            var Q0;
            Q0=sQuery(id+"F6.wireOp",VERTEX,"E42");
            var Q1;
            Q1=sQuery(id+"F6.wireOp",VERTEX,"E43");
            var Q2;
            Q2=makeQuery(id+"F1.opExtrude","SWEPT_BODY",BODY,{"disambiguationData":[OSD([sQuery(id+"F0.wireOp",EDGE,"E2"),sQuery(id+"F0.wireOp",EDGE,"E3"),sQuery(id+"F0.wireOp",EDGE,"E4"),sQuery(id+"F0.wireOp",EDGE,"E5"),sQuery(id+"F0.wireOp",EDGE,"E6.1.0.0"),sQuery(id+"F0.wireOp",EDGE,"E6.1.0.1"),sQuery(id+"F0.wireOp",EDGE,"E6.2.0.0"),sQuery(id+"F0.wireOp",EDGE,"E6.2.0.1"),sQuery(id+"F0.wireOp",EDGE,"E7.0.3.0"),sQuery(id+"F0.wireOp",EDGE,"E7.3.3.0"),sQuery(id+"F0.wireOp",EDGE,"E8.MirrorCS"),sQuery(id+"F0.wireOp",EDGE,"E9.MirrorCS"),sQuery(id+"F0.wireOp",EDGE,"E10.MirrorCS"),sQuery(id+"F0.wireOp",EDGE,"E11.MirrorCS"),sQuery(id+"F0.wireOp",EDGE,"E12.MirrorCS"),sQuery(id+"F0.wireOp",EDGE,"E13.MirrorCS"),sQuery(id+"F0.wireOp",EDGE,"E14.MirrorCS"),sQuery(id+"F0.wireOp",EDGE,"E15.MirrorCS"),sQuery(id+"F0.wireOp",EDGE,"E16.MirrorCS"),sQuery(id+"F0.wireOp",EDGE,"E17.MirrorCS"),sQuery(id+"F0.wireOp",EDGE,"E18.MirrorCS"),sQuery(id+"F0.wireOp",EDGE,"E19.MirrorCS"),sQuery(id+"F0.wireOp",EDGE,"E20.MirrorCS"),sQuery(id+"F0.wireOp",EDGE,"E21.MirrorCS"),sQuery(id+"F0.wireOp",EDGE,"E22.MirrorCS"),sQuery(id+"F0.wireOp",EDGE,"E23.MirrorCS"),sQuery(id+"F0.wireOp",EDGE,"E24.MirrorCS"),sQuery(id+"F0.wireOp",EDGE,"E25.MirrorCS"),sQuery(id+"F0.wireOp",EDGE,"E26.MirrorCS"),sQuery(id+"F0.wireOp",EDGE,"E27.MirrorCS"),sQuery(id+"F0.wireOp",EDGE,"E28.MirrorCS"),sQuery(id+"F0.wireOp",EDGE,"E29.MirrorCS"),sQuery(id+"F0.wireOp",EDGE,"E30.MirrorCS"),sQuery(id+"F0.wireOp",EDGE,"E31.MirrorCS"),sQuery(id+"F0.wireOp",EDGE,"E32.MirrorCS"),sQuery(id+"F0.wireOp",EDGE,"E33.MirrorCS"),sQuery(id+"F0.wireOp",EDGE,"E34.MirrorCS"),sQuery(id+"F0.wireOp",EDGE,"E35.MirrorCS"),sQuery(id+"F0.wireOp",EDGE,"E36.MirrorCS"),sQuery(id+"F0.wireOp",EDGE,"E37.MirrorCS")])]});
            hole(context, id + "F7", {"style" : HoleStyle.SIMPLE, "endStyle" : HoleEndStyle.THROUGH, "standardTappedOrClearance" : lookupTablePath({ "standard" : "ISO", "fit" : "Close", "size" : "M3", "type" : "Clearance" }), "standardBlindInLast" : lookupTablePath({ "fit" : "Close", "standard" : "ISO", "size" : "M3", "type" : "Clearance" }), "holeDiameter" : 3.15 * mm, "locations" : qUnion([Q0, Q1]), "scope" : qUnion([Q2]), "isTappedThrough" : true});
        }
    });
